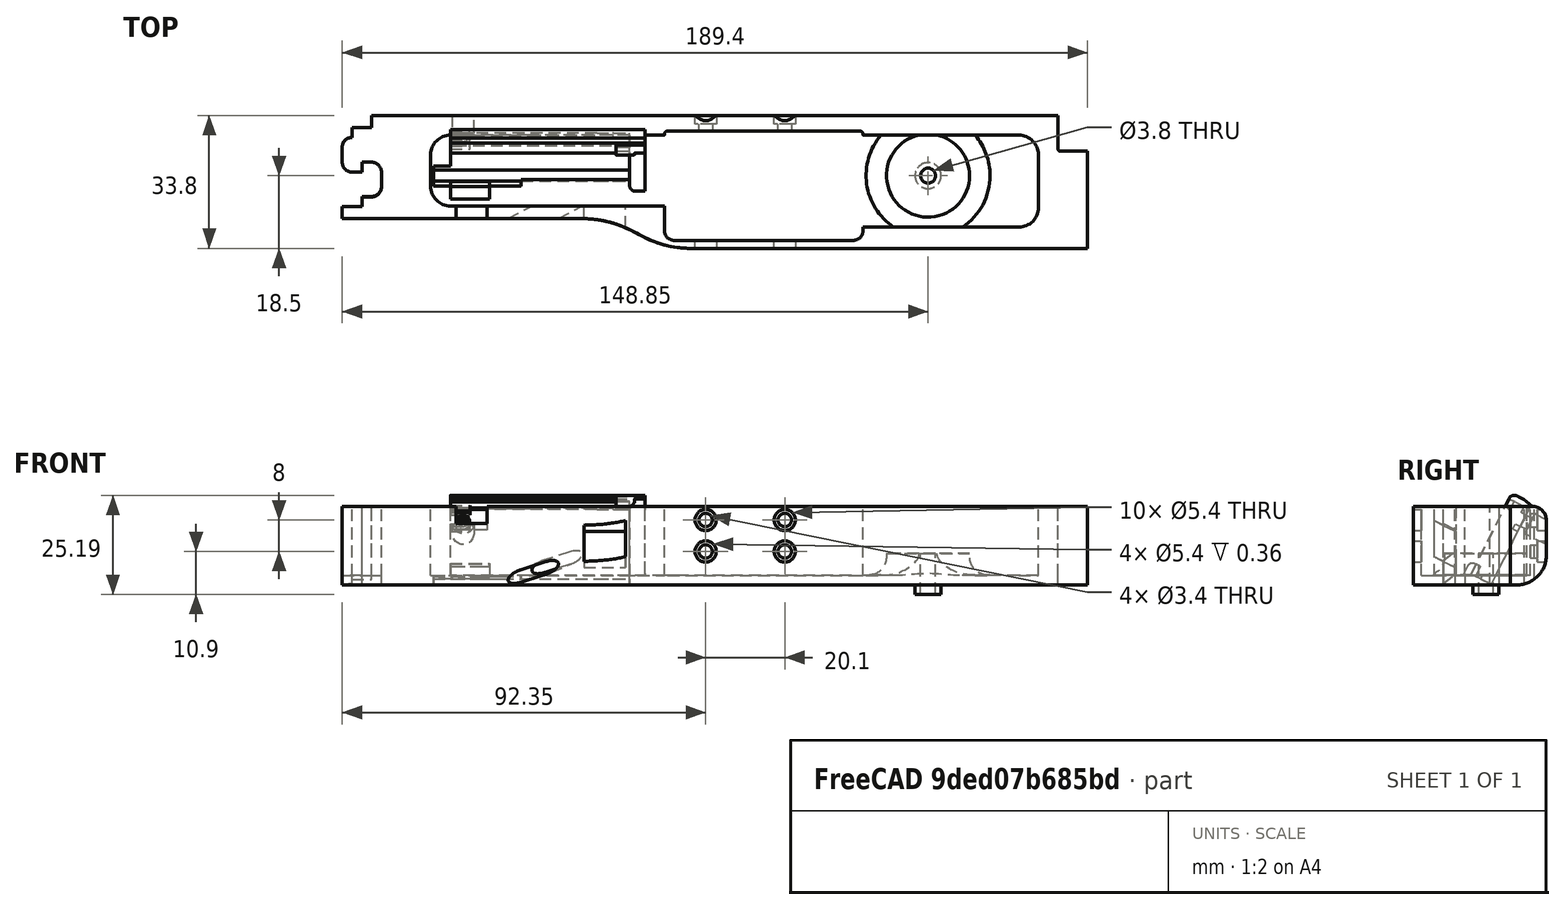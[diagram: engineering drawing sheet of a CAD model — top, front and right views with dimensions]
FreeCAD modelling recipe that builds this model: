
FCSTD DOCUMENT  (FreeCAD 0.19R0.19.2)
Label: v0_997
License: All rights reserved
LicenseURL: http://en.wikipedia.org/wiki/All_rights_reserved
objects: Sketcher::SketchObject×37, Part::Extrusion×31, Part::MultiFuse×19, Part::Cut×15, Part::Box×14, Part::Fillet×11, App::MeasureDistance×4, Part::Cylinder×4, Part::Revolution×1, Mesh::Feature×1
note: 132 computed .brp shape members not serialized (recipe doc carries the construction recipe); baked Part::Feature solids carry a one-line shape summary decoded from their .brp

FEATURE [Sketcher::SketchObject] Sketch
  FullyConstrained = true
  sketch-geometry (36):
    g0: LineSegment StartX=0 StartY=0 StartZ=0 EndX=154.4 EndY=0 EndZ=0
    g1: LineSegment StartX=154.4 StartY=0 StartZ=0 EndX=154.4 EndY=-7.6 EndZ=0
    g2: LineSegment StartX=32.5209 StartY=-26.2 StartZ=0 EndX=-7.5 EndY=-26.2 EndZ=0
    g3-g7: Circle x5 (B-spline internal-alignment scaffolding for g8; pole/knot coordinates omitted)
    g8: BSplineCurve PolesCount=5 KnotsCount=3 Degree=3 IsPeriodic=0
    g9: GeomPoint X=61.85 Y=-33.8 Z=0
    g10: GeomPoint X=47.185 Y=-29.9 Z=0
    g11: GeomPoint X=32.5209 Y=-26.2 Z=0
    g12: Circle CenterX=121.35 CenterY=-14.3 CenterZ=0 NormalX=0 NormalY=0 NormalZ=1 AngleXU=0 Radius=3.25
    g13: LineSegment StartX=-7.5 StartY=-26.2 StartZ=0 EndX=-27.5 EndY=-26.2 EndZ=0
    g14: LineSegment StartX=-20 StartY=0 StartZ=0 EndX=0 EndY=0 EndZ=0
    g15: LineSegment StartX=-25 StartY=-3.1 StartZ=0 EndX=-20 EndY=-3.1 EndZ=0
    g16: LineSegment StartX=-25 StartY=-3.1 StartZ=0 EndX=-25 EndY=-5.6 EndZ=0
    g17: LineSegment StartX=-27.5 StartY=-8.1 StartZ=0 EndX=-27.5 EndY=-11.85 EndZ=0
    g18: ArcOfCircle CenterX=-25 CenterY=-8.1 CenterZ=0 NormalX=0 NormalY=0 NormalZ=1 AngleXU=0 Radius=2.5 StartAngle=1.5708 EndAngle=3.14159
    g19: LineSegment StartX=-25 StartY=-14.35 StartZ=0 EndX=-22.5 EndY=-14.35 EndZ=0
    g20: ArcOfCircle CenterX=-25 CenterY=-11.85 CenterZ=0 NormalX=0 NormalY=0 NormalZ=1 AngleXU=0 Radius=2.5 StartAngle=3.14159 EndAngle=4.71239
    g21: LineSegment StartX=-22.5 StartY=-14.35 StartZ=0 EndX=-22.5 EndY=-11.85 EndZ=0
    g22: LineSegment StartX=-22.5 StartY=-11.85 StartZ=0 EndX=-20 EndY=-11.85 EndZ=0
    g23: ArcOfCircle CenterX=-20 CenterY=-14.35 CenterZ=0 NormalX=0 NormalY=0 NormalZ=1 AngleXU=0 Radius=2.5 StartAngle=8e-16 EndAngle=1.5708
    g24: LineSegment StartX=-17.5 StartY=-14.35 StartZ=0 EndX=-17.5 EndY=-18.1 EndZ=0
    g25: ArcOfCircle CenterX=-20 CenterY=-18.1 CenterZ=0 NormalX=0 NormalY=0 NormalZ=1 AngleXU=0 Radius=2.5 StartAngle=4.71239 EndAngle=6.28319
    g26: LineSegment StartX=-22.5 StartY=-20.6 StartZ=0 EndX=-20 EndY=-20.6 EndZ=0
    g27: LineSegment StartX=-22.5 StartY=-20.6 StartZ=0 EndX=-22.5 EndY=-23.1 EndZ=0
    g28: LineSegment StartX=-27.5 StartY=-23.1 StartZ=0 EndX=-22.5 EndY=-23.1 EndZ=0
    g29: LineSegment StartX=-20 StartY=-3.1 StartZ=0 EndX=-20 EndY=0 EndZ=0
    g30: LineSegment StartX=-27.5 StartY=-23.1 StartZ=0 EndX=-27.5 EndY=-26.2 EndZ=0
    g31: LineSegment StartX=154.4 StartY=-7.6 StartZ=0 EndX=154.4 EndY=-8.6 EndZ=0
    g32: ArcOfCircle CenterX=154.9 CenterY=-8.6 CenterZ=0 NormalX=0 NormalY=0 NormalZ=1 AngleXU=0 Radius=0.5 StartAngle=3.14159 EndAngle=4.71239
    g33: LineSegment StartX=154.9 StartY=-9.1 StartZ=0 EndX=161.9 EndY=-9.1 EndZ=0
    g34: LineSegment StartX=161.9 StartY=-9.1 StartZ=0 EndX=161.9 EndY=-33.8 EndZ=0
    g35: LineSegment StartX=161.9 StartY=-33.8 StartZ=0 EndX=61.85 EndY=-33.8 EndZ=0
  constraints (72):
    c: PointOnObject(g0,g-2)
    c: Horizontal(g0)
    c: Distance(g0) = 154.4
    c: DistanceY(g-1,g0) = 0
    c: Vertical(g1)
    c: Distance(g1) = 7.6
    c: Coincident(g1,g0)
    c: Horizontal(g2)
    c: Block(g2)
    c: Weight(g3) = 1
    c: Coincident(g8,g2)
    c: InternalAlignment(g3-g7 -> g8) x5
    c: InternalAlignment(g9,g8)
    c: InternalAlignment(g10,g8)
    c: InternalAlignment(g11,g8)
    c: Block(g12)
    c: Coincident(g13,g2)
    c: Horizontal(g13)
    c: Distance(g13) = 20
    c: Horizontal(g14)
    c: Distance(g14) = 20
    c: Coincident(g14,g0)
    c: Horizontal(g15)
    c: Vertical(g16)
    c: Coincident(g16,g15)
    c: Vertical(g17)
    c: Coincident(g18,g16)
    c: Block(g18)
    c: Coincident(g17,g18)
    c: Horizontal(g19)
    c: Coincident(g20,g17)
    c: Block(g20)
    c: Block(g19)
    c: Vertical(g21)
    c: Coincident(g21,g19)
    c: Horizontal(g22)
    c: Coincident(g22,g21)
    c: Coincident(g23,g22)
    c: Vertical(g24)
    c: Block(g23)
    c: Coincident(g24,g23)
    c: Coincident(g25,g24)
    c: Block(g25)
    c: Horizontal(g26)
    c: Coincident(g26,g25)
    c: Vertical(g27)
    c: Coincident(g27,g26)
    c: Horizontal(g28)
    c: Coincident(g28,g27)
    c: Block(g15)
    c: Block(g28)
    c: Coincident(g29,g15)
    c: Coincident(g29,g14)
    c: Vertical(g29)
    c: Coincident(g30,g28)
    c: Coincident(g30,g13)
    c: Vertical(g30)
    c: Vertical(g31)
    c: Distance(g31) = 1
    c: Coincident(g31,g1)
    c: Coincident(g32,g31)
    c: Block(g32)
    c: Coincident(g33,g32)
    c: Horizontal(g33)
    c: Coincident(g34,g33)
    c: Vertical(g34)
    c: Block(g34)
    c: Coincident(g35,g34)
    c: Horizontal(g35)
    c: Block(g35)
    c: Coincident(g8,g35)
    c: Block(g8)
FEATURE [Part::Extrusion] Extrude  label="mainBodyBaseExtrude"
  Base = -> Sketch
  Dir = (0,0,1)
  DirMode = 2
  FaceMakerClass = Part::FaceMakerBullseye
  LengthFwd = 2.4
  LengthRev = 0
  Solid = true
  Symmetric = false
FEATURE [Sketcher::SketchObject] Sketch001
  FullyConstrained = true
  sketch-geometry (75):
    g0: ArcOfCircle CenterX=144.4 CenterY=-10 CenterZ=0 NormalX=0 NormalY=0 NormalZ=1 AngleXU=0 Radius=5 StartAngle=4.345e-13 EndAngle=1.5708
    g1: LineSegment StartX=32.5209 StartY=-26.2 StartZ=0 EndX=-7.49911 EndY=-26.2 EndZ=0
    g2: LineSegment StartX=0 StartY=0 StartZ=0 EndX=154.4 EndY=0 EndZ=0
    g3-g7: Circle x5 (B-spline internal-alignment scaffolding for g8; pole/knot coordinates omitted)
    g8: BSplineCurve PolesCount=5 KnotsCount=3 Degree=3 IsPeriodic=0
    g9: GeomPoint X=61.85 Y=-33.8 Z=0
    g10: GeomPoint X=47.1857 Y=-29.9 Z=0
    g11: GeomPoint X=32.5209 Y=-26.2 Z=0
    g12: LineSegment StartX=154.4 StartY=0 StartZ=0 EndX=154.4 EndY=-7.6 EndZ=0
    g13: LineSegment StartX=20 StartY=-5 StartZ=0 EndX=54.35 EndY=-5 EndZ=0
    g14: LineSegment StartX=104.85 StartY=-5 StartZ=0 EndX=144.4 EndY=-5 EndZ=0
    g15: LineSegment StartX=54.35 StartY=-23 StartZ=0 EndX=20 EndY=-23 EndZ=0
    g16: LineSegment StartX=-27.4991 StartY=-26.2 StartZ=0 EndX=-7.49911 EndY=-26.2 EndZ=0
    g17: LineSegment StartX=-20 StartY=0 StartZ=0 EndX=0 EndY=0 EndZ=0
    g18: LineSegment StartX=-27.4991 StartY=-23.2 StartZ=0 EndX=-22.5 EndY=-23.2 EndZ=0
    g19: LineSegment StartX=-22.5 StartY=-20.7 StartZ=0 EndX=-22.5 EndY=-23.2 EndZ=0
    g20: LineSegment StartX=-22.5 StartY=-20.7 StartZ=0 EndX=-20 EndY=-20.7 EndZ=0
    g21: ArcOfCircle CenterX=-20 CenterY=-18.2 CenterZ=0 NormalX=0 NormalY=0 NormalZ=1 AngleXU=0 Radius=2.5 StartAngle=4.71239 EndAngle=6.28319
    g22: LineSegment StartX=-17.5 StartY=-14.4 StartZ=0 EndX=-17.5 EndY=-18.2 EndZ=0
    g23: ArcOfCircle CenterX=-20 CenterY=-14.4 CenterZ=0 NormalX=0 NormalY=0 NormalZ=1 AngleXU=0 Radius=2.5 StartAngle=9e-16 EndAngle=1.5708
    g24: LineSegment StartX=-22.5 StartY=-11.9 StartZ=0 EndX=-20 EndY=-11.9 EndZ=0
    g25: LineSegment StartX=-22.5 StartY=-14.4 StartZ=0 EndX=-22.5 EndY=-11.9 EndZ=0
    g26: LineSegment StartX=-25 StartY=-14.4 StartZ=0 EndX=-22.5 EndY=-14.4 EndZ=0
    g27: ArcOfCircle CenterX=-25 CenterY=-11.9 CenterZ=0 NormalX=0 NormalY=0 NormalZ=1 AngleXU=0 Radius=2.5 StartAngle=3.14159 EndAngle=4.71239
    g28: LineSegment StartX=-27.5 StartY=-8.1 StartZ=0 EndX=-27.5 EndY=-11.9 EndZ=0
    g29: ArcOfCircle CenterX=-25 CenterY=-8.1 CenterZ=0 NormalX=0 NormalY=0 NormalZ=1 AngleXU=0 Radius=2.5 StartAngle=1.5708 EndAngle=3.14159
    g30: LineSegment StartX=-25 StartY=-3.1 StartZ=0 EndX=-25 EndY=-5.6 EndZ=0
    g31: LineSegment StartX=-20 StartY=-3.1 StartZ=0 EndX=-25 EndY=-3.1 EndZ=0
    g32: LineSegment StartX=-20 StartY=0 StartZ=0 EndX=-20 EndY=-3.1 EndZ=0
    g33: LineSegment StartX=-27.4991 StartY=-26.2 StartZ=0 EndX=-27.4991 EndY=-23.2 EndZ=0
    g34: LineSegment StartX=4.09e-14 StartY=-5 StartZ=0 EndX=20 EndY=-5 EndZ=0
    g35: ArcOfCircle CenterX=7.1e-15 CenterY=-18 CenterZ=0 NormalX=0 NormalY=0 NormalZ=1 AngleXU=0 Radius=5 StartAngle=3.14159 EndAngle=4.71239
    g36: ArcOfCircle CenterX=4.26e-14 CenterY=-10 CenterZ=0 NormalX=0 NormalY=0 NormalZ=1 AngleXU=0 Radius=5 StartAngle=1.5708 EndAngle=3.14159
    g37: LineSegment StartX=-5 StartY=-18 StartZ=0 EndX=-5 EndY=-10 EndZ=0
    g38: LineSegment StartX=6.2e-15 StartY=-23 StartZ=0 EndX=20 EndY=-23 EndZ=0
    g39: LineSegment StartX=154.4 StartY=-7.6 StartZ=0 EndX=154.4 EndY=-8.6 EndZ=0
    g40: LineSegment StartX=154.9 StartY=-9.1 StartZ=0 EndX=161.9 EndY=-9.1 EndZ=0
    g41: ArcOfCircle CenterX=154.9 CenterY=-8.6 CenterZ=0 NormalX=0 NormalY=0 NormalZ=1 AngleXU=0 Radius=0.5 StartAngle=3.14159 EndAngle=4.71299
    g42: LineSegment StartX=104.85 StartY=-28.3916 StartZ=0 EndX=144.408 EndY=-28.3916 EndZ=0
    g43: LineSegment StartX=149.4 StartY=-10 StartZ=0 EndX=149.4 EndY=-23.4 EndZ=0
    g44: ArcOfCircle CenterX=144.408 CenterY=-23.4 CenterZ=0 NormalX=0 NormalY=0 NormalZ=1 AngleXU=0 Radius=4.99164 StartAngle=4.71239 EndAngle=6.28319
    g45: LineSegment StartX=104.85 StartY=-28.3916 StartZ=0 EndX=104.85 EndY=-28.7833 EndZ=0
    g46: LineSegment StartX=54.35 StartY=-28.7916 StartZ=0 EndX=54.35 EndY=-23 EndZ=0
    g47: LineSegment StartX=161.9 StartY=-33.8 StartZ=0 EndX=161.9 EndY=-9.1 EndZ=0
    g48: LineSegment StartX=61.85 StartY=-33.8 StartZ=0 EndX=161.9 EndY=-33.8 EndZ=0
    g49: Circle CenterX=54.35 CenterY=-28.7916 CenterZ=0 NormalX=0 NormalY=0 NormalZ=1 AngleXU=0 Radius=1
    g50: Circle CenterX=54.35 CenterY=-31.7916 CenterZ=0 NormalX=0 NormalY=0 NormalZ=1 AngleXU=0 Radius=1
    g51: Circle CenterX=57.35 CenterY=-31.7916 CenterZ=0 NormalX=0 NormalY=0 NormalZ=1 AngleXU=0 Radius=1
    g52: BSplineCurve PolesCount=3 KnotsCount=2 Degree=2 IsPeriodic=0
    g53: GeomPoint X=54.35 Y=-28.7916 Z=0
    g54: GeomPoint X=57.35 Y=-31.7916 Z=0
    g55: Circle CenterX=104.85 CenterY=-28.7833 CenterZ=0 NormalX=0 NormalY=0 NormalZ=1 AngleXU=0 Radius=1
    g56: Circle CenterX=104.85 CenterY=-31.7916 CenterZ=0 NormalX=0 NormalY=0 NormalZ=1 AngleXU=0 Radius=1
    g57: Circle CenterX=101.85 CenterY=-31.7916 CenterZ=0 NormalX=0 NormalY=0 NormalZ=1 AngleXU=0 Radius=1
    g58: BSplineCurve PolesCount=3 KnotsCount=2 Degree=2 IsPeriodic=0
    g59: GeomPoint X=104.85 Y=-28.7833 Z=0
    g60: GeomPoint X=101.85 Y=-31.7916 Z=0
    g61: LineSegment StartX=57.35 StartY=-31.7916 StartZ=0 EndX=101.85 EndY=-31.7916 EndZ=0
    g62: Circle CenterX=54.35 CenterY=-5 CenterZ=0 NormalX=0 NormalY=0 NormalZ=1 AngleXU=0 Radius=1
    g63: Circle CenterX=54.35 CenterY=-4 CenterZ=0 NormalX=0 NormalY=0 NormalZ=1 AngleXU=0 Radius=1
    g64: Circle CenterX=55.15 CenterY=-4 CenterZ=0 NormalX=0 NormalY=0 NormalZ=1 AngleXU=0 Radius=1
    g65: BSplineCurve PolesCount=3 KnotsCount=2 Degree=2 IsPeriodic=0
    g66: GeomPoint X=54.35 Y=-5 Z=0
    g67: GeomPoint X=55.15 Y=-4 Z=0
    g68: Circle CenterX=104.85 CenterY=-5 CenterZ=0 NormalX=0 NormalY=0 NormalZ=1 AngleXU=0 Radius=1
    g69: Circle CenterX=104.85 CenterY=-4 CenterZ=0 NormalX=0 NormalY=0 NormalZ=1 AngleXU=0 Radius=1
    g70: Circle CenterX=104.05 CenterY=-4 CenterZ=0 NormalX=0 NormalY=0 NormalZ=1 AngleXU=0 Radius=1
    g71: BSplineCurve PolesCount=3 KnotsCount=2 Degree=2 IsPeriodic=0
    g72: GeomPoint X=104.85 Y=-5 Z=0
    g73: GeomPoint X=104.05 Y=-4 Z=0
    g74: LineSegment StartX=104.05 StartY=-4 StartZ=0 EndX=55.15 EndY=-4 EndZ=0
  constraints (156):
    c: PointOnObject(g2,g-2)
    c: DistanceY(g-1,g2) = 0
    c: Block(g0)
    c: Horizontal(g1)
    c: Distance(g1) = 40.02
    c: Horizontal(g2)
    c: Block(g2)
    c: Weight(g3) = 1
    c: Equal(g3, g4-g7) x4
    c: Coincident(g8,g1)
    c: InternalAlignment(g3-g7 -> g8) x5
    c: InternalAlignment(g9,g8)
    c: InternalAlignment(g10,g8)
    c: InternalAlignment(g11,g8)
    c: Vertical(g12)
    c: Coincident(g12,g2)
    c: Distance(g12) = 7.6
    c: Block(g12)
    c: Horizontal(g13)
    c: Coincident(g14,g0)
    c: Horizontal(g14)
    c: Horizontal(g15)
    c: Horizontal(g16)
    c: Distance(g16) = 20
    c: Coincident(g1,g16)
    c: Horizontal(g17)
    c: Distance(g17) = 20
    c: Coincident(g17,g2)
    c: Horizontal(g31)
    c: Vertical(g30)
    c: Coincident(g29,g30)
    c: Vertical(g28)
    c: Block(g29)
    c: Coincident(g27,g28)
    c: Block(g27)
    c: Horizontal(g26)
    c: Coincident(g26,g27)
    c: Vertical(g25)
    c: Coincident(g25,g26)
    c: Horizontal(g24)
    c: Coincident(g23,g24)
    c: Block(g23)
    c: Vertical(g22)
    c: Coincident(g21,g22)
    c: Block(g21)
    c: Horizontal(g20)
    c: Coincident(g20,g21)
    c: Vertical(g19)
    c: Coincident(g19,g20)
    c: Horizontal(g18)
    c: Coincident(g18,g19)
    c: Coincident(g32,g17)
    c: Coincident(g32,g31)
    c: Vertical(g32)
    c: Coincident(g33,g16)
    c: Coincident(g33,g18)
    c: Vertical(g33)
    c: Block(g33)
    c: Block(g18)
    c: Block(g22)
    c: Block(g26)
    c: Block(g25)
    c: Block(g24)
    c: Block(g28)
    c: Block(g31)
    c: Block(g30)
    c: Horizontal(g34)
    c: Distance(g34) = 20
    c: Block(g35)
    c: Block(g36)
    c: Coincident(g37,g35)
    c: Coincident(g37,g36)
    c: Vertical(g37)
    c: Coincident(g38,g35)
    c: Coincident(g38,g15)
    c: Horizontal(g38)
    c: Block(g38)
    c: Block(g34)
    c: Block(g13)
    c: Vertical(g39)
    c: Distance(g39) = 1
    c: Coincident(g39,g12)
    c: Horizontal(g40)
    c: Coincident(g41,g39)
    c: Coincident(g41,g40)
    c: Block(g39)
    c: Block(g41)
    c: Horizontal(g42)
    c: Vertical(g43)
    c: Distance(g43) = 13.4
    c: Coincident(g43,g0)
    c: Block(g42)
    c: Block(g43)
    c: Coincident(g44,g43)
    c: Coincident(g44,g42)
    c: Block(g44)
    c: Distance(g15) = 34.35
    c: Coincident(g45,g42)
    c: Vertical(g45)
    c: Coincident(g46,g15)
    c: Vertical(g46)
    c: Coincident(g47,g40)
    c: Vertical(g47)
    c: Block(g47)
    c: Coincident(g48,g47)
    c: Horizontal(g48)
    c: Block(g48)
    c: Coincident(g8,g48)
    c: Block(g8)
    c: Coincident(g52,g46)
    c: Weight(g49) = 1
    c: Equal(g49,g50)
    c: Equal(g49,g51)
    c: InternalAlignment(g49,g52)
    c: InternalAlignment(g50,g52)
    c: InternalAlignment(g51,g52)
    c: InternalAlignment(g53,g52)
    c: InternalAlignment(g54,g52)
    c: Coincident(g58,g45)
    c: Weight(g55) = 1
    c: Equal(g55,g56)
    c: Equal(g55,g57)
    c: InternalAlignment(g55,g58)
    c: InternalAlignment(g56,g58)
    c: InternalAlignment(g57,g58)
    c: InternalAlignment(g59,g58)
    c: InternalAlignment(g60,g58)
    c: Block(g58)
    c: Block(g52)
    c: Coincident(g61,g52)
    c: Coincident(g61,g58)
    c: Horizontal(g61)
    c: Block(g14)
    c: Coincident(g65,g13)
    c: Weight(g62) = 1
    c: Equal(g62,g63)
    c: Equal(g62,g64)
    c: InternalAlignment(g62,g65)
    c: InternalAlignment(g63,g65)
    c: InternalAlignment(g64,g65)
    c: InternalAlignment(g66,g65)
    c: InternalAlignment(g67,g65)
    c: Block(g65)
    c: Coincident(g71,g14)
    c: Weight(g68) = 1
    c: Equal(g68,g69)
    c: Equal(g68,g70)
    c: InternalAlignment(g68,g71)
    c: InternalAlignment(g69,g71)
    c: InternalAlignment(g70,g71)
    c: InternalAlignment(g72,g71)
    c: InternalAlignment(g73,g71)
    c: Block(g71)
    c: Coincident(g74,g71)
    c: Coincident(g74,g65)
    c: Horizontal(g74)
FEATURE [Sketcher::SketchObject] Sketch005
  FullyConstrained = true
  Placement = pos=(0,0,0) rot=(1,0,0;1.5708rad)
  sketch-geometry (4):
    g0: Circle CenterX=84.95 CenterY=16.5 CenterZ=0 NormalX=0 NormalY=0 NormalZ=1 AngleXU=0 Radius=1.7
    g1: Circle CenterX=84.95 CenterY=8.5 CenterZ=0 NormalX=0 NormalY=0 NormalZ=1 AngleXU=0 Radius=1.7
    g2: Circle CenterX=64.85 CenterY=8.5 CenterZ=0 NormalX=0 NormalY=0 NormalZ=1 AngleXU=0 Radius=1.7
    g3: Circle CenterX=64.85 CenterY=16.5 CenterZ=0 NormalX=0 NormalY=0 NormalZ=1 AngleXU=0 Radius=1.7
  constraints (4):
    c: Block(g0)
    c: Block(g1)
    c: Block(g2)
    c: Block(g3)
FEATURE [Part::Extrusion] Extrude004  label="removeFromMainBodyToCreateScrewHolesForSolenoidExtrude004"
  Base = -> Sketch005
  Dir = (0,-1,1.1e-15)
  DirMode = 2
  FaceMakerClass = Part::FaceMakerBullseye
  LengthFwd = 10
  LengthRev = 0
  Solid = true
  Symmetric = false
FEATURE [Sketcher::SketchObject] Sketch004
  FullyConstrained = true
  Placement = pos=(0,0,0) rot=(1,0,0;1.5708rad)
  sketch-geometry (12):
    g0: LineSegment StartX=15.75 StartY=2.5 StartZ=0 EndX=15.75 EndY=0 EndZ=0
    g1: Circle CenterX=15.75 CenterY=2.5 CenterZ=0 NormalX=0 NormalY=0 NormalZ=1 AngleXU=0 Radius=1
    g2: Circle CenterX=10.55 CenterY=2.5 CenterZ=0 NormalX=0 NormalY=0 NormalZ=1 AngleXU=0 Radius=1
    g3: Circle CenterX=10.55 CenterY=8 CenterZ=0 NormalX=0 NormalY=0 NormalZ=1 AngleXU=0 Radius=1
    g4: BSplineCurve PolesCount=3 KnotsCount=2 Degree=2 IsPeriodic=0
    g5: GeomPoint X=15.75 Y=2.5 Z=0
    g6: GeomPoint X=10.55 Y=8 Z=0
    g7: LineSegment StartX=1.9 StartY=8 StartZ=0 EndX=10.55 EndY=8 EndZ=0
    g8: LineSegment StartX=1.9 StartY=-2.4 StartZ=0 EndX=1.9 EndY=8 EndZ=0
    g9: LineSegment StartX=3.30092 StartY=-2.4 StartZ=0 EndX=3.30092 EndY=0 EndZ=0
    g10: LineSegment StartX=15.75 StartY=0 StartZ=0 EndX=3.30092 EndY=0 EndZ=0
    g11: LineSegment StartX=3.30092 StartY=-2.4 StartZ=0 EndX=1.9 EndY=-2.4 EndZ=0
  constraints (26):
    c: Vertical(g0)
    c: Distance(g0) = 2.5
    c: Coincident(g4,g0)
    c: Weight(g1) = 1
    c: Equal(g1,g2)
    c: Equal(g1,g3)
    c: InternalAlignment(g1,g4)
    c: InternalAlignment(g2,g4)
    c: InternalAlignment(g3,g4)
    c: InternalAlignment(g5,g4)
    c: InternalAlignment(g6,g4)
    c: Block(g4)
    c: Coincident(g7,g4)
    c: Horizontal(g7)
    c: Vertical(g8)
    c: Coincident(g8,g7)
    c: Block(g8)
    c: Vertical(g9)
    c: Coincident(g10,g0)
    c: PointOnObject(g10,g-1)
    c: Horizontal(g10)
    c: Coincident(g10,g9)
    c: Block(g9)
    c: Coincident(g11,g9)
    c: Coincident(g11,g8)
    c: Horizontal(g11)
FEATURE [Sketcher::SketchObject] Sketch007
  FullyConstrained = true
  Placement = pos=(0,-14.3,2.37) rot=(-1,0,0;2.03453rad)
  sketch-geometry (6):
    g0: LineSegment StartX=0 StartY=0 StartZ=0 EndX=45.5 EndY=0 EndZ=0
    g1: LineSegment StartX=0 StartY=0 StartZ=0 EndX=0 EndY=-21.2 EndZ=0
    g2: LineSegment StartX=45.5 StartY=0 StartZ=0 EndX=49.5 EndY=0 EndZ=0
    g3: LineSegment StartX=49.5 StartY=0 StartZ=0 EndX=49.5 EndY=-21.2 EndZ=0
    g4: LineSegment StartX=49.5 StartY=-21.2 StartZ=0 EndX=0 EndY=-21.2 EndZ=0
    g5: Circle CenterX=3.25 CenterY=-18.05 CenterZ=0 NormalX=0 NormalY=0 NormalZ=1 AngleXU=0 Radius=1.6
  constraints (15):
    c: Coincident(g0,g-1)
    c: Horizontal(g0)
    c: Distance(g0) = 45.5
    c: Coincident(g1,g0)
    c: Vertical(g1)
    c: Horizontal(g2)
    c: Distance(g2) = 4
    c: Coincident(g2,g0)
    c: Coincident(g3,g2)
    c: Vertical(g3)
    c: Block(g3)
    c: Coincident(g4,g3)
    c: Horizontal(g4)
    c: Coincident(g4,g1)
    c: Block(g5)
FEATURE [Part::Extrusion] Extrude005  label="solenoidDriverHolderExtrude005"
  Base = -> Sketch007
  Dir = (0,0.894389,-0.447291)
  DirMode = 2
  FaceMakerClass = Part::FaceMakerBullseye
  LengthFwd = 10
  LengthRev = 0
  Placement = pos=(0,0,-2) rot=(0,0,1;0rad)
  Solid = true
  Symmetric = false
FEATURE [Sketcher::SketchObject] Sketch008
  FullyConstrained = false
  Placement = pos=(0,-4.3,-2.6) rot=(-1,0,0;2.03453rad)
  sketch-geometry (1):
    g0: Circle CenterX=42.25 CenterY=-3.15 CenterZ=0 NormalX=0 NormalY=0 NormalZ=1 AngleXU=0 Radius=4.5
FEATURE [Sketcher::SketchObject] Sketch009
  FullyConstrained = true
  Placement = pos=(0,-4.3,-2.6) rot=(-1,0,0;2.03453rad)
  sketch-geometry (1):
    g0: Circle CenterX=3.25 CenterY=-18.0217 CenterZ=0 NormalX=0 NormalY=0 NormalZ=1 AngleXU=0 Radius=2.8
  constraints (1):
    c: Block(g0)
FEATURE [Sketcher::SketchObject] Sketch010
  FullyConstrained = true
  Placement = pos=(0,-14.3,2.37) rot=(-1,0,0;2.03453rad)
  sketch-geometry (1):
    g0: Circle CenterX=3.25 CenterY=-18.05 CenterZ=0 NormalX=0 NormalY=0 NormalZ=1 AngleXU=0 Radius=1.6
  constraints (1):
    c: Block(g0)
FEATURE [Part::Extrusion] Extrude008  label="removeFromScrewHole3"
  Base = -> Sketch010
  Dir = (0,0.894389,-0.447291)
  DirMode = 2
  FaceMakerClass = Part::FaceMakerBullseye
  LengthFwd = -25
  LengthRev = 0
  Placement = pos=(0,4,-4) rot=(0,0,1;0rad)
  Solid = true
  Symmetric = false
FEATURE [Sketcher::SketchObject] Sketch011
  FullyConstrained = true
  Placement = pos=(0,-14.3,2.37) rot=(-1,0,0;2.03453rad)
  sketch-geometry (4):
    g0: LineSegment StartX=49.5 StartY=-21.2 StartZ=0 EndX=49.5 EndY=-22.8 EndZ=0
    g1: LineSegment StartX=49.5 StartY=-22.8 StartZ=0 EndX=0.002238 EndY=-22.8 EndZ=0
    g2: LineSegment StartX=0.002238 StartY=-21.2 StartZ=0 EndX=0.002238 EndY=-22.8 EndZ=0
    g3: LineSegment StartX=49.5 StartY=-21.2 StartZ=0 EndX=0.002238 EndY=-21.2 EndZ=0
  constraints (10):
    c: Vertical(g0)
    c: Distance(g0) = 1.6
    c: Coincident(g1,g0)
    c: Horizontal(g1)
    c: Vertical(g2)
    c: Coincident(g2,g1)
    c: Coincident(g3,g0)
    c: Coincident(g3,g2)
    c: Horizontal(g3)
    c: Block(g3)
FEATURE [Part::Extrusion] Extrude009  label="solenoidDriverTopLipFront"
  Base = -> Sketch011
  Dir = (0,0.894389,-0.447291)
  DirMode = 2
  FaceMakerClass = Part::FaceMakerBullseye
  LengthFwd = -2
  LengthRev = 0
  Placement = pos=(0,-2.9,-0.35) rot=(0,0,1;0rad)
  Solid = true
  Symmetric = false
FEATURE [Sketcher::SketchObject] Sketch012
  FullyConstrained = true
  Placement = pos=(0,-14.3,2.37) rot=(-1,0,0;2.03453rad)
  sketch-geometry (4):
    g0: LineSegment StartX=49.5 StartY=-21.2 StartZ=0 EndX=49.5 EndY=-22.8 EndZ=0
    g1: LineSegment StartX=49.5 StartY=-22.8 StartZ=0 EndX=0.002238 EndY=-22.8 EndZ=0
    g2: LineSegment StartX=0.002238 StartY=-21.2 StartZ=0 EndX=0.002238 EndY=-22.8 EndZ=0
    g3: LineSegment StartX=49.5 StartY=-21.2 StartZ=0 EndX=0.002238 EndY=-21.2 EndZ=0
  constraints (10):
    c: Vertical(g0)
    c: Distance(g0) = 1.6
    c: Coincident(g1,g0)
    c: Horizontal(g1)
    c: Vertical(g2)
    c: Coincident(g2,g1)
    c: Coincident(g3,g0)
    c: Coincident(g3,g2)
    c: Horizontal(g3)
    c: Block(g3)
FEATURE [Part::Extrusion] Extrude010  label="solenoidDriverTopLipLowerExtrude010"
  Base = -> Sketch012
  Dir = (0,0.894389,-0.447291)
  DirMode = 2
  FaceMakerClass = Part::FaceMakerBullseye
  LengthFwd = 5.05
  LengthRev = 0
  Solid = true
  Symmetric = false
FEATURE [Sketcher::SketchObject] Sketch015
  FullyConstrained = true
  Placement = pos=(0,-14.3,2.37) rot=(-1,0,0;2.03453rad)
  sketch-geometry (4):
    g0: LineSegment StartX=0 StartY=1.5 StartZ=0 EndX=0 EndY=0 EndZ=0
    g1: LineSegment StartX=0 StartY=1.5 StartZ=0 EndX=5 EndY=1.5 EndZ=0
    g2: LineSegment StartX=5 StartY=1.5 StartZ=0 EndX=5 EndY=0 EndZ=0
    g3: LineSegment StartX=0 StartY=0 StartZ=0 EndX=5 EndY=0 EndZ=0
  constraints (13):
    c: Vertical(g0)
    c: Distance(g0) = 1.5
    c: Horizontal(g1)
    c: Distance(g1) = 5
    c: Coincident(g1,g0)
    c: Vertical(g2)
    c: Distance(g2) = 1.5
    c: Coincident(g2,g1)
    c: Block(g1)
    c: Block(g2)
    c: Block(g0)
    c: Coincident(g3,g0)
    c: Coincident(g3,g2)
FEATURE [Part::Extrusion] Extrude013  label="solenoidDriverBottomLipTopExtrude012"
  Base = -> Sketch015
  Dir = (0,0.894389,-0.447291)
  DirMode = 2
  FaceMakerClass = Part::FaceMakerBullseye
  LengthFwd = -6.5
  LengthRev = 0
  Placement = pos=(0,-14.15,19.65) rot=(1,0,0;1.5708rad)
  Solid = true
  Symmetric = false
FEATURE [Sketcher::SketchObject] Sketch016
  FullyConstrained = true
  Placement = pos=(0,0,0) rot=(1,0,0;1.5708rad)
  sketch-geometry (4):
    g0: Circle CenterX=84.15 CenterY=16.5 CenterZ=0 NormalX=0 NormalY=0 NormalZ=1 AngleXU=0 Radius=2.7
    g1: Circle CenterX=64.05 CenterY=16.5 CenterZ=0 NormalX=0 NormalY=0 NormalZ=1 AngleXU=0 Radius=2.7
    g2: Circle CenterX=64.05 CenterY=8.5 CenterZ=0 NormalX=0 NormalY=0 NormalZ=1 AngleXU=0 Radius=2.7
    g3: Circle CenterX=84.15 CenterY=8.5 CenterZ=0 NormalX=0 NormalY=0 NormalZ=1 AngleXU=0 Radius=2.7
  constraints (4):
    c: Block(g0)
    c: Block(g1)
    c: Block(g3)
    c: Block(g2)
FEATURE [Part::Extrusion] Extrude014  label="removeFromMainBodyToCreateScrewHoleCounterSinks"
  Base = -> Sketch016
  Dir = (0,-1,1.1e-15)
  DirMode = 2
  FaceMakerClass = Part::FaceMakerBullseye
  LengthFwd = 1.9
  LengthRev = 0
  Placement = pos=(0.8,-0.36,0) rot=(0,0,1;0rad)
  Solid = true
  Symmetric = false
FEATURE [Part::Extrusion] Extrude015  label="removeFromScrewHole2Extrude007"
  Base = -> Sketch009
  Dir = (0,0.894389,-0.447291)
  DirMode = 2
  FaceMakerClass = Part::FaceMakerBullseye
  LengthFwd = 10
  LengthRev = 0
  Placement = pos=(0,-8,2) rot=(0,0,1;0rad)
  Solid = true
  Symmetric = false
FEATURE [Sketcher::SketchObject] Sketch017
  FullyConstrained = true
  Placement = pos=(0,-14.3,2.37) rot=(-1,0,0;2.03453rad)
  sketch-geometry (4):
    g0: LineSegment StartX=0 StartY=1.5 StartZ=0 EndX=0 EndY=0 EndZ=0
    g1: LineSegment StartX=0 StartY=1.5 StartZ=0 EndX=5 EndY=1.5 EndZ=0
    g2: LineSegment StartX=5 StartY=1.5 StartZ=0 EndX=5 EndY=0 EndZ=0
    g3: LineSegment StartX=0 StartY=0 StartZ=0 EndX=5 EndY=0 EndZ=0
  constraints (13):
    c: Vertical(g0)
    c: Distance(g0) = 1.5
    c: Horizontal(g1)
    c: Distance(g1) = 5
    c: Coincident(g1,g0)
    c: Vertical(g2)
    c: Distance(g2) = 1.5
    c: Coincident(g2,g1)
    c: Block(g1)
    c: Block(g2)
    c: Block(g0)
    c: Coincident(g3,g0)
    c: Coincident(g3,g2)
FEATURE [Part::Extrusion] Extrude016  label="solenoidDriverBottomLipTopExtrude013"
  Base = -> Sketch017
  Dir = (0,0.894389,-0.447291)
  DirMode = 2
  FaceMakerClass = Part::FaceMakerBullseye
  LengthFwd = -6.5
  LengthRev = 0
  Placement = pos=(0,-15.45,20.3) rot=(1,0,0;1.5708rad)
  Solid = true
  Symmetric = false
FEATURE [Part::Fillet] Fillet005  label="solenoidDriverBottomLipTopFillet005"
  Base = -> Extrude016
  Edges = 1 edges r=1.4: [Edge6]
FEATURE [Sketcher::SketchObject] Sketch018
  FullyConstrained = true
  Placement = pos=(38.5,-14.3,2.37) rot=(-1,0,0;2.03453rad)
  sketch-geometry (4):
    g0: LineSegment StartX=11 StartY=0 StartZ=0 EndX=11 EndY=1.5 EndZ=0
    g1: LineSegment StartX=11 StartY=0 StartZ=0 EndX=3.6 EndY=0 EndZ=0
    g2: LineSegment StartX=3.6 StartY=0 StartZ=0 EndX=3.6 EndY=1.5 EndZ=0
    g3: LineSegment StartX=11 StartY=1.5 StartZ=0 EndX=3.6 EndY=1.5 EndZ=0
  constraints (12):
    c: PointOnObject(g0,g-1)
    c: Vertical(g0)
    c: Distance(g0) = 1.5
    c: Horizontal(g1)
    c: Distance(g1) = 7.4
    c: Coincident(g1,g0)
    c: Block(g0)
    c: Coincident(g2,g1)
    c: Vertical(g2)
    c: Coincident(g3,g0)
    c: Horizontal(g3)
    c: Coincident(g2,g3)
FEATURE [Part::Extrusion] Extrude017
  Base = -> Sketch018
  Dir = (0,0.894389,-0.447291)
  DirMode = 2
  FaceMakerClass = Part::FaceMakerBullseye
  LengthFwd = 4
  LengthRev = 0
  Placement = pos=(0,-8.212,34.025) rot=(1,0,0;1.5708rad)
  Solid = true
  Symmetric = false
FEATURE [Sketcher::SketchObject] Sketch019
  FullyConstrained = true
  Placement = pos=(0,0,0) rot=(1,0,0;1.5708rad)
  sketch-geometry (4):
    g0: Circle CenterX=84.95 CenterY=8.5 CenterZ=0 NormalX=0 NormalY=0 NormalZ=1 AngleXU=0 Radius=2.7
    g1: Circle CenterX=64.85 CenterY=8.5 CenterZ=0 NormalX=0 NormalY=0 NormalZ=1 AngleXU=0 Radius=2.7
    g2: Circle CenterX=64.85 CenterY=16.5 CenterZ=0 NormalX=0 NormalY=0 NormalZ=1 AngleXU=0 Radius=2.7
    g3: Circle CenterX=84.95 CenterY=16.5 CenterZ=0 NormalX=0 NormalY=0 NormalZ=1 AngleXU=0 Radius=2.7
  constraints (4):
    c: Block(g3)
    c: Block(g2)
    c: Block(g0)
    c: Block(g1)
FEATURE [Part::Extrusion] Extrude019  label="removeSolenoidAdjusterHoles"
  Base = -> Sketch019
  Dir = (0,-1,1.1e-15)
  DirMode = 2
  FaceMakerClass = Part::FaceMakerBullseye
  LengthFwd = 6
  LengthRev = 0
  Placement = pos=(0,-30,0) rot=(0,0,1;0rad)
  Solid = true
  Symmetric = false
FEATURE [Sketcher::SketchObject] Sketch020
  FullyConstrained = true
  Placement = pos=(0,-14.3,2.37) rot=(-1,0,0;2.03453rad)
  sketch-geometry (6):
    g0: LineSegment StartX=45.5 StartY=-21.2 StartZ=0 EndX=49.5 EndY=-21.2 EndZ=0
    g1: LineSegment StartX=45.5 StartY=0 StartZ=0 EndX=49.5 EndY=0 EndZ=0
    g2: LineSegment StartX=49.5 StartY=0 StartZ=0 EndX=49.5 EndY=-21.2 EndZ=0
    g3: LineSegment StartX=4 StartY=0 StartZ=0 EndX=4 EndY=-21.2 EndZ=0
    g4: LineSegment StartX=45.5 StartY=-21.2 StartZ=0 EndX=4 EndY=-21.2 EndZ=0
    g5: LineSegment StartX=4 StartY=0 StartZ=0 EndX=45.5 EndY=0 EndZ=0
  constraints (16):
    c: Horizontal(g0)
    c: Distance(g0) = 4
    c: Horizontal(g1)
    c: Distance(g1) = 4
    c: Coincident(g2,g1)
    c: Coincident(g2,g0)
    c: Vertical(g2)
    c: Block(g2)
    c: Vertical(g3)
    c: Coincident(g4,g0)
    c: Horizontal(g4)
    c: Coincident(g4,g3)
    c: Coincident(g5,g1)
    c: Horizontal(g5)
    c: Block(g3)
    c: Block(g5)
FEATURE [Part::Box] Box  label="Cube"
  AttacherType = Attacher::AttachEngine3D
  Height = 10
  Length = 190
  Placement = pos=(-30,0,0) rot=(0,0,1;0rad)
  Width = 10
FEATURE [Part::Fillet] Fillet008
  Base = -> Box
  Edges = 1 edges r=7.5: [Edge11]
FEATURE [Part::Box] Box001  label="Cube001"
  AttacherType = Attacher::AttachEngine3D
  Height = 10
  Length = 190
  Placement = pos=(-35,0,0) rot=(0,0,1;0rad)
  Width = 10
FEATURE [Part::Cut] Cut  label="filletMain"
  Base = -> Box001
  Placement = pos=(0,-10,0) rot=(0,0,1;0rad)
  Tool = -> Fillet008
FEATURE [Part::Box] Box002  label="Cube002"
  AttacherType = Attacher::AttachEngine3D
  Height = 30
  Length = 190
  Placement = pos=(-20,0,0) rot=(0,0,1;0rad)
  Width = 10
FEATURE [Part::Box] Box003  label="Cube003"
  AttacherType = Attacher::AttachEngine3D
  Height = 10
  Length = 190
  Placement = pos=(-90,-50,-10) rot=(0,0,1;0rad)
  Width = 50
FEATURE [Sketcher::SketchObject] Sketch021
  FullyConstrained = true
  Placement = pos=(0,-14.3,2.37) rot=(-1,0,0;2.03453rad)
  sketch-geometry (6):
    g0: LineSegment StartX=41.65 StartY=-3.15 StartZ=0 EndX=38.95 EndY=-3.15 EndZ=0
    g1: LineSegment StartX=36.25 StartY=-3.15 StartZ=0 EndX=38.95 EndY=-3.15 EndZ=0
    g2: LineSegment StartX=41.65 StartY=-3.15 StartZ=0 EndX=41.65 EndY=-7.15 EndZ=0
    g3: LineSegment StartX=38.95 StartY=-7.15 StartZ=0 EndX=41.65 EndY=-7.15 EndZ=0
    g4: LineSegment StartX=38.95 StartY=-7.15 StartZ=0 EndX=36.25 EndY=-7.15 EndZ=0
    g5: LineSegment StartX=36.25 StartY=-3.15 StartZ=0 EndX=36.25 EndY=-7.15 EndZ=0
  constraints (16):
    c: Horizontal(g0)
    c: Distance(g0) = 2.7
    c: Horizontal(g1)
    c: Distance(g1) = 2.7
    c: Coincident(g1,g0)
    c: Block(g0)
    c: Coincident(g2,g0)
    c: Vertical(g2)
    c: Horizontal(g3)
    c: Coincident(g3,g2)
    c: Horizontal(g4)
    c: Coincident(g5,g1)
    c: Vertical(g5)
    c: Coincident(g5,g4)
    c: Block(g3)
    c: Block(g4)
FEATURE [Sketcher::SketchObject] Sketch022
  FullyConstrained = true
  Placement = pos=(0,-14.3,2.37) rot=(-1,0,0;2.03453rad)
  sketch-geometry (6):
    g0: LineSegment StartX=41.65 StartY=-3.15 StartZ=0 EndX=38.95 EndY=-3.15 EndZ=0
    g1: LineSegment StartX=36.25 StartY=-3.15 StartZ=0 EndX=38.95 EndY=-3.15 EndZ=0
    g2: LineSegment StartX=41.65 StartY=-3.15 StartZ=0 EndX=41.65 EndY=-7.15 EndZ=0
    g3: LineSegment StartX=38.95 StartY=-7.15 StartZ=0 EndX=41.65 EndY=-7.15 EndZ=0
    g4: LineSegment StartX=38.95 StartY=-7.15 StartZ=0 EndX=36.25 EndY=-7.15 EndZ=0
    g5: LineSegment StartX=36.25 StartY=-3.15 StartZ=0 EndX=36.25 EndY=-7.15 EndZ=0
  constraints (16):
    c: Horizontal(g0)
    c: Distance(g0) = 2.7
    c: Horizontal(g1)
    c: Distance(g1) = 2.7
    c: Coincident(g1,g0)
    c: Block(g0)
    c: Coincident(g2,g0)
    c: Vertical(g2)
    c: Horizontal(g3)
    c: Coincident(g3,g2)
    c: Horizontal(g4)
    c: Coincident(g5,g1)
    c: Vertical(g5)
    c: Coincident(g5,g4)
    c: Block(g3)
    c: Block(g4)
FEATURE [Sketcher::SketchObject] Sketch024
  FullyConstrained = true
  Placement = pos=(0,-14.3,2.37) rot=(-1,0,0;2.03453rad)
  sketch-geometry (4):
    g0: LineSegment StartX=49.5 StartY=-21.2 StartZ=0 EndX=49.5 EndY=-22.8 EndZ=0
    g1: LineSegment StartX=49.5 StartY=-22.8 StartZ=0 EndX=0.002238 EndY=-22.8 EndZ=0
    g2: LineSegment StartX=0.002238 StartY=-21.2 StartZ=0 EndX=0.002238 EndY=-22.8 EndZ=0
    g3: LineSegment StartX=49.5 StartY=-21.2 StartZ=0 EndX=0.002238 EndY=-21.2 EndZ=0
  constraints (10):
    c: Vertical(g0)
    c: Distance(g0) = 1.6
    c: Coincident(g1,g0)
    c: Horizontal(g1)
    c: Vertical(g2)
    c: Coincident(g2,g1)
    c: Coincident(g3,g0)
    c: Coincident(g3,g2)
    c: Horizontal(g3)
    c: Block(g3)
FEATURE [Sketcher::SketchObject] Sketch025
  FullyConstrained = true
  Placement = pos=(0,-14.3,2.37) rot=(-1,0,0;2.03453rad)
  sketch-geometry (4):
    g0: LineSegment StartX=0 StartY=1.5 StartZ=0 EndX=0 EndY=0 EndZ=0
    g1: LineSegment StartX=0 StartY=1.5 StartZ=0 EndX=5 EndY=1.5 EndZ=0
    g2: LineSegment StartX=5 StartY=1.5 StartZ=0 EndX=5 EndY=0 EndZ=0
    g3: LineSegment StartX=0 StartY=0 StartZ=0 EndX=5 EndY=0 EndZ=0
  constraints (13):
    c: Vertical(g0)
    c: Distance(g0) = 1.5
    c: Horizontal(g1)
    c: Distance(g1) = 5
    c: Coincident(g1,g0)
    c: Vertical(g2)
    c: Distance(g2) = 1.5
    c: Coincident(g2,g1)
    c: Block(g1)
    c: Block(g2)
    c: Block(g0)
    c: Coincident(g3,g0)
    c: Coincident(g3,g2)
FEATURE [Part::Extrusion] Extrude022  label="solenoidDriverBottomLipTopExtrude014"
  Base = -> Sketch025
  Dir = (0,0.894389,-0.447291)
  DirMode = 2
  FaceMakerClass = Part::FaceMakerBullseye
  LengthFwd = -6.5
  LengthRev = 0
  Placement = pos=(0,-15.45,20.3) rot=(1,0,0;1.5708rad)
  Solid = true
  Symmetric = false
FEATURE [Part::Fillet] Fillet013  label="solenoidDriverBottomLipTopFillet006"
  Base = -> Extrude022
  Edges = 1 edges r=1.4: [Edge6]
  Placement = pos=(5,0,0) rot=(0,0,1;0rad)
FEATURE [Sketcher::SketchObject] Sketch026
  FullyConstrained = true
  Placement = pos=(0,-14.3,2.37) rot=(-1,0,0;2.03453rad)
  sketch-geometry (4):
    g0: LineSegment StartX=0 StartY=1.5 StartZ=0 EndX=0 EndY=0 EndZ=0
    g1: LineSegment StartX=0 StartY=1.5 StartZ=0 EndX=5 EndY=1.5 EndZ=0
    g2: LineSegment StartX=5 StartY=1.5 StartZ=0 EndX=5 EndY=0 EndZ=0
    g3: LineSegment StartX=0 StartY=0 StartZ=0 EndX=5 EndY=0 EndZ=0
  constraints (13):
    c: Vertical(g0)
    c: Distance(g0) = 1.5
    c: Horizontal(g1)
    c: Distance(g1) = 5
    c: Coincident(g1,g0)
    c: Vertical(g2)
    c: Distance(g2) = 1.5
    c: Coincident(g2,g1)
    c: Block(g1)
    c: Block(g2)
    c: Block(g0)
    c: Coincident(g3,g0)
    c: Coincident(g3,g2)
FEATURE [Part::Extrusion] Extrude023  label="solenoidDriverBottomLipTopExtrude015"
  Base = -> Sketch026
  Dir = (0,0.894389,-0.447291)
  DirMode = 2
  FaceMakerClass = Part::FaceMakerBullseye
  LengthFwd = -6.5
  LengthRev = 0
  Placement = pos=(5,-14.15,19.65) rot=(1,0,0;1.5708rad)
  Solid = true
  Symmetric = false
FEATURE [Sketcher::SketchObject] Sketch027
  FullyConstrained = true
  Placement = pos=(0,-14.3,2.37) rot=(-1,0,0;2.03453rad)
  sketch-geometry (5):
    g0: LineSegment StartX=45.5 StartY=-21.2 StartZ=0 EndX=49.5 EndY=-21.2 EndZ=0
    g1: LineSegment StartX=49.5 StartY=0 StartZ=0 EndX=49.5 EndY=-21.2 EndZ=0
    g2: LineSegment StartX=49.5 StartY=0 StartZ=0 EndX=49.5 EndY=1.6 EndZ=0
    g3: LineSegment StartX=45.5 StartY=-21.2 StartZ=0 EndX=45.5 EndY=1.6 EndZ=0
    g4: LineSegment StartX=49.5 StartY=1.6 StartZ=0 EndX=45.5 EndY=1.6 EndZ=0
  constraints (14):
    c: Horizontal(g0)
    c: Distance(g0) = 4
    c: Coincident(g1,g0)
    c: Vertical(g1)
    c: Block(g1)
    c: Vertical(g2)
    c: Distance(g2) = 1.6
    c: Block(g2)
    c: Coincident(g3,g0)
    c: Vertical(g3)
    c: Coincident(g4,g2)
    c: Horizontal(g4)
    c: Block(g0)
    c: Coincident(g3,g4)
FEATURE [Part::Extrusion] Extrude024
  Base = -> Sketch027
  Dir = (0,0.894389,-0.447291)
  DirMode = 2
  FaceMakerClass = Part::FaceMakerBullseye
  LengthFwd = 6.34
  LengthRev = 0
  Placement = pos=(0,-5.59,1) rot=(0,0,1;0rad)
  Solid = true
  Symmetric = false
FEATURE [Part::Fillet] Fillet014  label="solenoidDriverSideBarFillet014"
  Base = -> Extrude024
  Edges = 1 edges r=1.4: [Edge14]
  Placement = pos=(0,0.9,-0.45) rot=(0,0,1;0rad)
FEATURE [Part::Revolution] Revolve  label="mainScrewStandRevolve"
  Angle = 360
  Axis = (0,0,1)
  Base = (0,0,0)
  FaceMakerClass = Part::FaceMakerBullseye
  Placement = pos=(121.35,-15.3,0) rot=(0,0,1;0rad)
  Solid = true
  Source = -> Sketch004
  Symmetric = false
FEATURE [Part::Extrusion] Extrude021  label="solenoidDriverTopLipLowerExtrude011"
  Base = -> Sketch024
  Dir = (0,0.894389,-0.447291)
  DirMode = 2
  FaceMakerClass = Part::FaceMakerBullseye
  LengthFwd = 5.05
  LengthRev = 0
  Solid = true
  Symmetric = false
FEATURE [Part::Fillet] Fillet012  label="solenoidDriverTopLipLowerFillet004"
  Base = -> Extrude021
  Edges = 1 edges r=1.2: [Edge7]
  Placement = pos=(0,-0.9,-1.35) rot=(0,0,1;0rad)
FEATURE [Part::Fillet] Fillet003  label="solenoidDriverTopLipLowerFillet003"
  Base = -> Extrude010
  Edges = 1 edges r=1.2: [Edge7]
  Placement = pos=(0,-3,-0.3) rot=(0,0,1;0rad)
FEATURE [Part::Extrusion] Extrude025  label="mainBodyUpperExtrude025"
  Base = -> Sketch001
  Dir = (0,0,1)
  DirMode = 2
  FaceMakerClass = Part::FaceMakerBullseye
  LengthFwd = 20
  LengthRev = 0
  Solid = true
  Symmetric = false
FEATURE [Part::MultiFuse] Fusion  label="solenoidDriverBottomLipFusion"
  Placement = pos=(0,-1.6,0) rot=(0,0,1;0rad)
  Shapes = -> [Fillet005,Fillet013,Extrude023,Extrude013]
FEATURE [Sketcher::SketchObject] Sketch028
  FullyConstrained = true
  Placement = pos=(0,-14.3,2.37) rot=(-1,0,0;2.03453rad)
  sketch-geometry (4):
    g0: LineSegment StartX=0 StartY=1.5 StartZ=0 EndX=0 EndY=0 EndZ=0
    g1: LineSegment StartX=0 StartY=1.5 StartZ=0 EndX=5 EndY=1.5 EndZ=0
    g2: LineSegment StartX=5 StartY=1.5 StartZ=0 EndX=5 EndY=0 EndZ=0
    g3: LineSegment StartX=0 StartY=0 StartZ=0 EndX=5 EndY=0 EndZ=0
  constraints (13):
    c: Vertical(g0)
    c: Distance(g0) = 1.5
    c: Horizontal(g1)
    c: Distance(g1) = 5
    c: Coincident(g1,g0)
    c: Vertical(g2)
    c: Distance(g2) = 1.5
    c: Coincident(g2,g1)
    c: Block(g1)
    c: Block(g2)
    c: Block(g0)
    c: Coincident(g3,g0)
    c: Coincident(g3,g2)
FEATURE [Part::Extrusion] Extrude026  label="solenoidDriverBottomLipTopExtrude016"
  Base = -> Sketch028
  Dir = (0,0.894389,-0.447291)
  DirMode = 2
  FaceMakerClass = Part::FaceMakerBullseye
  LengthFwd = -6.5
  LengthRev = 0
  Placement = pos=(5,-14.15,19.65) rot=(1,0,0;1.5708rad)
  Solid = true
  Symmetric = false
FEATURE [Sketcher::SketchObject] Sketch029
  FullyConstrained = true
  Placement = pos=(0,-14.3,2.37) rot=(-1,0,0;2.03453rad)
  sketch-geometry (4):
    g0: LineSegment StartX=0 StartY=1.5 StartZ=0 EndX=0 EndY=0 EndZ=0
    g1: LineSegment StartX=0 StartY=1.5 StartZ=0 EndX=5 EndY=1.5 EndZ=0
    g2: LineSegment StartX=5 StartY=1.5 StartZ=0 EndX=5 EndY=0 EndZ=0
    g3: LineSegment StartX=0 StartY=0 StartZ=0 EndX=5 EndY=0 EndZ=0
  constraints (13):
    c: Vertical(g0)
    c: Distance(g0) = 1.5
    c: Horizontal(g1)
    c: Distance(g1) = 5
    c: Coincident(g1,g0)
    c: Vertical(g2)
    c: Distance(g2) = 1.5
    c: Coincident(g2,g1)
    c: Block(g1)
    c: Block(g2)
    c: Block(g0)
    c: Coincident(g3,g0)
    c: Coincident(g3,g2)
FEATURE [Part::Extrusion] Extrude027  label="solenoidDriverBottomLipTopExtrude017"
  Base = -> Sketch029
  Dir = (0,0.894389,-0.447291)
  DirMode = 2
  FaceMakerClass = Part::FaceMakerBullseye
  LengthFwd = -6.5
  LengthRev = 0
  Placement = pos=(0,-14.15,19.65) rot=(1,0,0;1.5708rad)
  Solid = true
  Symmetric = false
FEATURE [Sketcher::SketchObject] Sketch030
  FullyConstrained = true
  Placement = pos=(0,-14.3,2.37) rot=(-1,0,0;2.03453rad)
  sketch-geometry (4):
    g0: LineSegment StartX=0 StartY=1.5 StartZ=0 EndX=0 EndY=0 EndZ=0
    g1: LineSegment StartX=0 StartY=1.5 StartZ=0 EndX=5 EndY=1.5 EndZ=0
    g2: LineSegment StartX=5 StartY=1.5 StartZ=0 EndX=5 EndY=0 EndZ=0
    g3: LineSegment StartX=0 StartY=0 StartZ=0 EndX=5 EndY=0 EndZ=0
  constraints (13):
    c: Vertical(g0)
    c: Distance(g0) = 1.5
    c: Horizontal(g1)
    c: Distance(g1) = 5
    c: Coincident(g1,g0)
    c: Vertical(g2)
    c: Distance(g2) = 1.5
    c: Coincident(g2,g1)
    c: Block(g1)
    c: Block(g2)
    c: Block(g0)
    c: Coincident(g3,g0)
    c: Coincident(g3,g2)
FEATURE [Sketcher::SketchObject] Sketch031
  FullyConstrained = true
  Placement = pos=(0,-14.3,2.37) rot=(-1,0,0;2.03453rad)
  sketch-geometry (6):
    g0: LineSegment StartX=45.5 StartY=-21.2 StartZ=0 EndX=49.5 EndY=-21.2 EndZ=0
    g1: LineSegment StartX=45.5 StartY=0 StartZ=0 EndX=49.5 EndY=0 EndZ=0
    g2: LineSegment StartX=49.5 StartY=0 StartZ=0 EndX=49.5 EndY=-21.2 EndZ=0
    g3: LineSegment StartX=4 StartY=0 StartZ=0 EndX=4 EndY=-21.2 EndZ=0
    g4: LineSegment StartX=45.5 StartY=-21.2 StartZ=0 EndX=4 EndY=-21.2 EndZ=0
    g5: LineSegment StartX=4 StartY=0 StartZ=0 EndX=45.5 EndY=0 EndZ=0
  constraints (16):
    c: Horizontal(g0)
    c: Distance(g0) = 4
    c: Horizontal(g1)
    c: Distance(g1) = 4
    c: Coincident(g2,g1)
    c: Coincident(g2,g0)
    c: Vertical(g2)
    c: Block(g2)
    c: Vertical(g3)
    c: Coincident(g4,g0)
    c: Horizontal(g4)
    c: Coincident(g4,g3)
    c: Coincident(g5,g1)
    c: Horizontal(g5)
    c: Block(g3)
    c: Block(g5)
FEATURE [Part::Extrusion] Extrude028  label="removeFromSolenoidDriverMainExtrude021"
  Base = -> Sketch031
  Dir = (0,0.894389,-0.447291)
  DirMode = 2
  FaceMakerClass = Part::FaceMakerBullseye
  LengthFwd = 3.1
  LengthRev = 0
  Placement = pos=(-4,-2.42,-0.8) rot=(0,0,1;0rad)
  Solid = true
  Symmetric = false
FEATURE [Part::Extrusion] Extrude029  label="solenoidDriverBottomLipTopExtrude018"
  Base = -> Sketch030
  Dir = (0,0.894389,-0.447291)
  DirMode = 2
  FaceMakerClass = Part::FaceMakerBullseye
  LengthFwd = -6.5
  LengthRev = 0
  Placement = pos=(5,-14.15,19.65) rot=(1,0,0;1.5708rad)
  Solid = true
  Symmetric = false
FEATURE [Sketcher::SketchObject] Sketch032
  FullyConstrained = true
  Placement = pos=(0,-14.3,2.37) rot=(-1,0,0;2.03453rad)
  sketch-geometry (4):
    g0: LineSegment StartX=0 StartY=1.5 StartZ=0 EndX=0 EndY=0 EndZ=0
    g1: LineSegment StartX=0 StartY=1.5 StartZ=0 EndX=5 EndY=1.5 EndZ=0
    g2: LineSegment StartX=5 StartY=1.5 StartZ=0 EndX=5 EndY=0 EndZ=0
    g3: LineSegment StartX=0 StartY=0 StartZ=0 EndX=5 EndY=0 EndZ=0
  constraints (13):
    c: Vertical(g0)
    c: Distance(g0) = 1.5
    c: Horizontal(g1)
    c: Distance(g1) = 5
    c: Coincident(g1,g0)
    c: Vertical(g2)
    c: Distance(g2) = 1.5
    c: Coincident(g2,g1)
    c: Block(g1)
    c: Block(g2)
    c: Block(g0)
    c: Coincident(g3,g0)
    c: Coincident(g3,g2)
FEATURE [Part::Extrusion] Extrude030  label="solenoidDriverBottomLipTopExtrude019"
  Base = -> Sketch032
  Dir = (0,0.894389,-0.447291)
  DirMode = 2
  FaceMakerClass = Part::FaceMakerBullseye
  LengthFwd = -6.5
  LengthRev = 0
  Placement = pos=(0,-14.15,19.65) rot=(1,0,0;1.5708rad)
  Solid = true
  Symmetric = false
FEATURE [Part::MultiFuse] Fusion004
  Placement = pos=(0,1.4,2.65) rot=(0,0,1;0rad)
  Shapes = -> [Extrude029,Extrude030]
FEATURE [Part::MultiFuse] Fusion003
  Placement = pos=(-2.3,0,0) rot=(0,0,1;0rad)
  Shapes = -> [Extrude028,Fusion004]
FEATURE [Sketcher::SketchObject] Sketch033
  FullyConstrained = true
  Placement = pos=(0,-14.3,2.37) rot=(-1,0,0;2.03453rad)
  sketch-geometry (4):
    g0: LineSegment StartX=0 StartY=1.5 StartZ=0 EndX=0 EndY=0 EndZ=0
    g1: LineSegment StartX=0 StartY=1.5 StartZ=0 EndX=5 EndY=1.5 EndZ=0
    g2: LineSegment StartX=5 StartY=1.5 StartZ=0 EndX=5 EndY=0 EndZ=0
    g3: LineSegment StartX=0 StartY=0 StartZ=0 EndX=5 EndY=0 EndZ=0
  constraints (13):
    c: Vertical(g0)
    c: Distance(g0) = 1.5
    c: Horizontal(g1)
    c: Distance(g1) = 5
    c: Coincident(g1,g0)
    c: Vertical(g2)
    c: Distance(g2) = 1.5
    c: Coincident(g2,g1)
    c: Block(g1)
    c: Block(g2)
    c: Block(g0)
    c: Coincident(g3,g0)
    c: Coincident(g3,g2)
FEATURE [Sketcher::SketchObject] Sketch034
  FullyConstrained = true
  Placement = pos=(0,-14.3,2.37) rot=(-1,0,0;2.03453rad)
  sketch-geometry (4):
    g0: LineSegment StartX=0 StartY=1.5 StartZ=0 EndX=0 EndY=0 EndZ=0
    g1: LineSegment StartX=0 StartY=1.5 StartZ=0 EndX=5 EndY=1.5 EndZ=0
    g2: LineSegment StartX=5 StartY=1.5 StartZ=0 EndX=5 EndY=0 EndZ=0
    g3: LineSegment StartX=0 StartY=0 StartZ=0 EndX=5 EndY=0 EndZ=0
  constraints (13):
    c: Vertical(g0)
    c: Distance(g0) = 1.5
    c: Horizontal(g1)
    c: Distance(g1) = 5
    c: Coincident(g1,g0)
    c: Vertical(g2)
    c: Distance(g2) = 1.5
    c: Coincident(g2,g1)
    c: Block(g1)
    c: Block(g2)
    c: Block(g0)
    c: Coincident(g3,g0)
    c: Coincident(g3,g2)
FEATURE [Part::Extrusion] Extrude020  label="removeFromSolenoidDriverMainExtrude020"
  Base = -> Sketch020
  Dir = (0,0.894389,-0.447291)
  DirMode = 2
  FaceMakerClass = Part::FaceMakerBullseye
  LengthFwd = 3.1
  LengthRev = 0
  Placement = pos=(-4,-2.42,-0.8) rot=(0,0,1;0rad)
  Solid = true
  Symmetric = false
FEATURE [Part::Fillet] Fillet
  Base = -> Fusion003
  Edges = 1 edges r=10: [Edge5]
  Placement = pos=(-2,0,0) rot=(0,0,1;0rad)
FEATURE [Part::MultiFuse] Fusion001
  Placement = pos=(0,1.4,2.65) rot=(0,0,1;0rad)
  Shapes = -> [Extrude026,Extrude027]
FEATURE [Part::MultiFuse] Fusion002
  Shapes = -> [Extrude020,Fusion001]
FEATURE [Sketcher::SketchObject] Sketch035
  FullyConstrained = true
  Placement = pos=(0,-14.3,2.37) rot=(-1,0,0;2.03453rad)
  sketch-geometry (4):
    g0: LineSegment StartX=0 StartY=1.5 StartZ=0 EndX=0 EndY=0 EndZ=0
    g1: LineSegment StartX=0 StartY=1.5 StartZ=0 EndX=5 EndY=1.5 EndZ=0
    g2: LineSegment StartX=5 StartY=1.5 StartZ=0 EndX=5 EndY=0 EndZ=0
    g3: LineSegment StartX=0 StartY=0 StartZ=0 EndX=5 EndY=0 EndZ=0
  constraints (13):
    c: Vertical(g0)
    c: Distance(g0) = 1.5
    c: Horizontal(g1)
    c: Distance(g1) = 5
    c: Coincident(g1,g0)
    c: Vertical(g2)
    c: Distance(g2) = 1.5
    c: Coincident(g2,g1)
    c: Block(g1)
    c: Block(g2)
    c: Block(g0)
    c: Coincident(g3,g0)
    c: Coincident(g3,g2)
FEATURE [Sketcher::SketchObject] Sketch036
  FullyConstrained = true
  Placement = pos=(0,-14.3,2.37) rot=(-1,0,0;2.03453rad)
  sketch-geometry (4):
    g0: LineSegment StartX=0 StartY=1.5 StartZ=0 EndX=0 EndY=0 EndZ=0
    g1: LineSegment StartX=0 StartY=1.5 StartZ=0 EndX=5 EndY=1.5 EndZ=0
    g2: LineSegment StartX=5 StartY=1.5 StartZ=0 EndX=5 EndY=0 EndZ=0
    g3: LineSegment StartX=0 StartY=0 StartZ=0 EndX=5 EndY=0 EndZ=0
  constraints (13):
    c: Vertical(g0)
    c: Distance(g0) = 1.5
    c: Horizontal(g1)
    c: Distance(g1) = 5
    c: Coincident(g1,g0)
    c: Vertical(g2)
    c: Distance(g2) = 1.5
    c: Coincident(g2,g1)
    c: Block(g1)
    c: Block(g2)
    c: Block(g0)
    c: Coincident(g3,g0)
    c: Coincident(g3,g2)
FEATURE [Part::Extrusion] Extrude031  label="solenoidDriverBottomLipTopExtrude020"
  Base = -> Sketch035
  Dir = (0,0.894389,-0.447291)
  DirMode = 2
  FaceMakerClass = Part::FaceMakerBullseye
  LengthFwd = -6.5
  LengthRev = 0
  Placement = pos=(5,-14.15,19.65) rot=(1,0,0;1.5708rad)
  Solid = true
  Symmetric = false
FEATURE [Part::Extrusion] Extrude032  label="solenoidDriverBottomLipTopExtrude021"
  Base = -> Sketch036
  Dir = (0,0.894389,-0.447291)
  DirMode = 2
  FaceMakerClass = Part::FaceMakerBullseye
  LengthFwd = -6.5
  LengthRev = 0
  Placement = pos=(0,-14.15,19.65) rot=(1,0,0;1.5708rad)
  Solid = true
  Symmetric = false
FEATURE [Part::MultiFuse] Fusion009
  Placement = pos=(8,1.4,2.65) rot=(0,0,1;0rad)
  Shapes = -> [Extrude031,Extrude032]
FEATURE [Part::MultiFuse] Fusion010  label="removeFromSolenoidDriver"
  Shapes = -> [Fusion009,Fillet,Fusion002]
FEATURE [Sketcher::SketchObject] Sketch037
  FullyConstrained = true
  Placement = pos=(0,0,0) rot=(1,0,0;1.5708rad)
  sketch-geometry (4):
    g0: Circle CenterX=64.05 CenterY=16.5 CenterZ=0 NormalX=0 NormalY=0 NormalZ=1 AngleXU=0 Radius=2.7
    g1: Circle CenterX=64.05 CenterY=8.5 CenterZ=0 NormalX=0 NormalY=0 NormalZ=1 AngleXU=0 Radius=2.7
    g2: Circle CenterX=84.15 CenterY=8.5 CenterZ=0 NormalX=0 NormalY=0 NormalZ=1 AngleXU=0 Radius=2.7
    g3: Circle CenterX=84.15 CenterY=16.5 CenterZ=0 NormalX=0 NormalY=0 NormalZ=1 AngleXU=0 Radius=2.7
  constraints (4):
    c: Block(g2)
    c: Block(g3)
    c: Block(g0)
    c: Block(g1)
FEATURE [Part::Extrusion] Extrude033  label="removeFromMainBodyToCreateScrewHoleCounterSinks001"
  Base = -> Sketch037
  Dir = (0,-1,1.1e-15)
  DirMode = 2
  FaceMakerClass = Part::FaceMakerBullseye
  LengthFwd = 1.9
  LengthRev = 0
  Placement = pos=(0.8,0,0) rot=(0,0,1;0rad)
  Solid = true
  Symmetric = false
FEATURE [Part::MultiFuse] Fusion011  label="removeFromMainBodyToCreateScrewHoleCounterSinks001Fusion011"
  Shapes = -> [Extrude014,Extrude033]
FEATURE [Sketcher::SketchObject] Sketch038
  FullyConstrained = true
  Placement = pos=(0,-14.3,2.37) rot=(-1,0,0;2.03453rad)
  sketch-geometry (4):
    g0: LineSegment StartX=33.9 StartY=-9.7 StartZ=0 EndX=33.9 EndY=-1.5 EndZ=0
    g1: LineSegment StartX=33.9 StartY=-1.5 StartZ=0 EndX=44.5 EndY=-1.5 EndZ=0
    g2: LineSegment StartX=33.9 StartY=-9.7 StartZ=0 EndX=44.5 EndY=-9.7 EndZ=0
    g3: LineSegment StartX=44.5 StartY=-1.5 StartZ=0 EndX=44.5 EndY=-9.7 EndZ=0
  constraints (10):
    c: Vertical(g0)
    c: Coincident(g1,g0)
    c: Horizontal(g1)
    c: Block(g1)
    c: Block(g0)
    c: Coincident(g2,g0)
    c: Horizontal(g2)
    c: Coincident(g3,g1)
    c: Coincident(g3,g2)
    c: Vertical(g3)
FEATURE [Part::Extrusion] Extrude034
  Base = -> Sketch038
  Dir = (0,0.894389,-0.447291)
  DirMode = 2
  FaceMakerClass = Part::FaceMakerBullseye
  LengthFwd = 16
  LengthRev = 0
  Placement = pos=(0,-22,7) rot=(0,0,1;0rad)
  Solid = true
  Symmetric = false
FEATURE [Sketcher::SketchObject] Sketch039
  FullyConstrained = true
  Placement = pos=(0,-14.3,2.37) rot=(-1,0,0;2.03453rad)
  sketch-geometry (4):
    g0: LineSegment StartX=5.5 StartY=-7.7 StartZ=0 EndX=13.3 EndY=-7.7 EndZ=0
    g1: LineSegment StartX=13.3 StartY=-7.7 StartZ=0 EndX=13.3 EndY=-13.1 EndZ=0
    g2: LineSegment StartX=13.3 StartY=-13.1 StartZ=0 EndX=5.5 EndY=-13.1 EndZ=0
    g3: LineSegment StartX=5.5 StartY=-7.7 StartZ=0 EndX=5.5 EndY=-13.1 EndZ=0
  constraints (12):
    c: Horizontal(g0)
    c: Distance(g0) = 7.8
    c: Coincident(g1,g0)
    c: Vertical(g1)
    c: Distance(g1) = 5.4
    c: Coincident(g2,g1)
    c: Horizontal(g2)
    c: Vertical(g3)
    c: Coincident(g3,g2)
    c: Block(g0)
    c: Block(g2)
    c: Block(g3)
FEATURE [Part::Extrusion] Extrude035  label="removeToMakeHoleForConnectorExtrude035"
  Base = -> Sketch039
  Dir = (0,0.894389,-0.447291)
  DirMode = 2
  FaceMakerClass = Part::FaceMakerBullseye
  LengthFwd = 15
  LengthRev = 0
  Placement = pos=(-4,-22,9.6469) rot=(0,0,1;0rad)
  Solid = true
  Symmetric = false
FEATURE [App::MeasureDistance] Distance  label="Distance: 4.00 mm"
  Distance = 4.00184
  P1 = (119.349,-15.3,8)
  P2 = (123.351,-15.3,8)
FEATURE [App::MeasureDistance] Distance001  label="Distance: 3.80 mm"
  Distance = 3.8
  P1 = (119.45,-15.3,8)
  P2 = (123.25,-15.3,8)
FEATURE [Part::Fillet] Fillet015
  Base = -> Extrude009
  Edges = 1 edges r=1.59: [Edge7]
FEATURE [Part::Fillet] Fillet016
  Base = -> Extrude017
  Edges = 1 edges r=1.49: [Edge12]
FEATURE [Part::Fillet] Fillet017
  Base = -> Fillet016
  Edges = 1 edges r=1.45: [Edge8]
FEATURE [Part::MultiFuse] Fusion012  label="main"
  Shapes = -> [Extrude,Revolve,Extrude005,Fillet003,Fillet012,Fillet014,Extrude025,Fusion,Fillet015,Fillet017]
FEATURE [Part::Cut] Cut001
  Base = -> Fusion012
  Tool = -> Box003
FEATURE [Part::Cut] Cut002
  Base = -> Cut001
  Tool = -> Box002
FEATURE [Part::Cut] Cut003
  Base = -> Cut002
  Tool = -> Cut
FEATURE [Part::Cut] Cut004
  Base = -> Cut003
  Tool = -> Extrude019
FEATURE [Part::Cut] Cut005
  Base = -> Cut004
  Tool = -> Fusion011
FEATURE [Part::Cut] Cut006
  Base = -> Cut005
  Tool = -> Extrude004
FEATURE [Part::Cut] Cut007
  Base = -> Cut006
  Tool = -> Extrude015
FEATURE [Part::Cut] Cut008
  Base = -> Cut007
  Tool = -> Extrude008
FEATURE [Part::Cut] Cut009
  Base = -> Cut008
  Tool = -> Fusion010
FEATURE [App::MeasureDistance] Distance002  label="Distance: 2.05 mm"
  Distance = 2.05453
  P1 = (1.5,-23.0732,21.402)
  P2 = (6e-15,-23,20)
FEATURE [Part::Cut] Cut010
  Base = -> Cut009
  Tool = -> Extrude035
FEATURE [Part::Cut] Cut011
  Base = -> Cut010
  Tool = -> Extrude034
FEATURE [Part::Box] Box004  label="Cube004"
  AttacherType = Attacher::AttachEngine3D
  Height = 10
  Length = 200
  Placement = pos=(-30,0,0) rot=(0,0,1;0rad)
  Width = 10
FEATURE [Part::Fillet] Fillet020
  Base = -> Box004
  Edges = 1 edges r=3.6: [Edge12]
FEATURE [Part::Box] Box005  label="Cube005"
  AttacherType = Attacher::AttachEngine3D
  Height = 10
  Length = 198
  Placement = pos=(-30,0,0) rot=(0,0,1;0rad)
  Width = 10
FEATURE [Part::Cut] Cut012
  Base = -> Box005
  Tool = -> Fillet020
FEATURE [Part::Box] Box006  label="Cube006"
  AttacherType = Attacher::AttachEngine3D
  Height = 5
  Length = 200
  Placement = pos=(-30,6.4,10) rot=(1,0,0;0rad)
  Width = 5
FEATURE [Part::Box] Box007  label="Cube007"
  AttacherType = Attacher::AttachEngine3D
  Height = 5
  Length = 200
  Placement = pos=(-30,6.4,10) rot=(1,0,0;0.872665rad)
  Width = 5
FEATURE [Part::MultiFuse] Fusion013  label="removeFromMainFusion013"
  Placement = pos=(0,-10,10) rot=(0,0,1;0rad)
  Shapes = -> [Box007,Box006,Cut012]
FEATURE [Mesh::Feature] v0_98_Cut013  label="v0_98-Cut013"
FEATURE [App::MeasureDistance] Distance003  label="Distance: 7.18 mm"
  Distance = 7.17719
  P1 = (117.773,-15.3145,-2.4)
  P2 = (124.951,-15.2973,-2.4)
FEATURE [Sketcher::SketchObject] Sketch040
  FullyConstrained = true
  Placement = pos=(0,-14.3,2.37) rot=(-1,0,0;2.03453rad)
  sketch-geometry (4):
    g0: LineSegment StartX=0 StartY=1.5 StartZ=0 EndX=0 EndY=0 EndZ=0
    g1: LineSegment StartX=0 StartY=1.5 StartZ=0 EndX=5 EndY=1.5 EndZ=0
    g2: LineSegment StartX=5 StartY=1.5 StartZ=0 EndX=5 EndY=0 EndZ=0
    g3: LineSegment StartX=0 StartY=0 StartZ=0 EndX=5 EndY=0 EndZ=0
  constraints (13):
    c: Vertical(g0)
    c: Distance(g0) = 1.5
    c: Horizontal(g1)
    c: Distance(g1) = 5
    c: Coincident(g1,g0)
    c: Vertical(g2)
    c: Distance(g2) = 1.5
    c: Coincident(g2,g1)
    c: Block(g1)
    c: Block(g2)
    c: Block(g0)
    c: Coincident(g3,g0)
    c: Coincident(g3,g2)
FEATURE [Part::Extrusion] Extrude036
  Base = -> Sketch040
  Dir = (0,0.894389,-0.447291)
  DirMode = 2
  FaceMakerClass = Part::FaceMakerBullseye
  LengthFwd = 1.4
  LengthRev = 0
  Placement = pos=(0,8.25,17.58) rot=(0,0,1;0rad)
  Solid = true
  Symmetric = false
FEATURE [Sketcher::SketchObject] Sketch041
  FullyConstrained = true
  Placement = pos=(0,-14.3,2.37) rot=(-1,0,0;2.03453rad)
  sketch-geometry (4):
    g0: LineSegment StartX=0 StartY=1.5 StartZ=0 EndX=0 EndY=0 EndZ=0
    g1: LineSegment StartX=0 StartY=1.5 StartZ=0 EndX=5 EndY=1.5 EndZ=0
    g2: LineSegment StartX=5 StartY=1.5 StartZ=0 EndX=5 EndY=0 EndZ=0
    g3: LineSegment StartX=0 StartY=0 StartZ=0 EndX=5 EndY=0 EndZ=0
  constraints (13):
    c: Vertical(g0)
    c: Distance(g0) = 1.5
    c: Horizontal(g1)
    c: Distance(g1) = 5
    c: Coincident(g1,g0)
    c: Vertical(g2)
    c: Distance(g2) = 1.5
    c: Coincident(g2,g1)
    c: Block(g1)
    c: Block(g2)
    c: Block(g0)
    c: Coincident(g3,g0)
    c: Coincident(g3,g2)
FEATURE [Part::Extrusion] Extrude037
  Base = -> Sketch041
  Dir = (0,0.894389,-0.447291)
  DirMode = 2
  FaceMakerClass = Part::FaceMakerBullseye
  LengthFwd = 1.4
  LengthRev = 0
  Placement = pos=(0,6.11,13.33) rot=(0,0,1;0rad)
  Solid = true
  Symmetric = false
FEATURE [Part::MultiFuse] Fusion014  label="screwSpacerFusion014"
  Shapes = -> [Extrude037,Extrude036]
FEATURE [Sketcher::SketchObject] Sketch042
  FullyConstrained = true
  Placement = pos=(0,-14.3,2.37) rot=(-1,0,0;2.03453rad)
  sketch-geometry (4):
    g0: LineSegment StartX=0 StartY=1.5 StartZ=0 EndX=0 EndY=0 EndZ=0
    g1: LineSegment StartX=0 StartY=1.5 StartZ=0 EndX=5 EndY=1.5 EndZ=0
    g2: LineSegment StartX=5 StartY=1.5 StartZ=0 EndX=5 EndY=0 EndZ=0
    g3: LineSegment StartX=0 StartY=0 StartZ=0 EndX=5 EndY=0 EndZ=0
  constraints (13):
    c: Vertical(g0)
    c: Distance(g0) = 1.5
    c: Horizontal(g1)
    c: Distance(g1) = 5
    c: Coincident(g1,g0)
    c: Vertical(g2)
    c: Distance(g2) = 1.5
    c: Coincident(g2,g1)
    c: Block(g1)
    c: Block(g2)
    c: Block(g0)
    c: Coincident(g3,g0)
    c: Coincident(g3,g2)
FEATURE [Part::Extrusion] Extrude038
  Base = -> Sketch042
  Dir = (0,0.894389,-0.447291)
  DirMode = 2
  FaceMakerClass = Part::FaceMakerBullseye
  LengthFwd = 1.4
  LengthRev = 0
  Placement = pos=(0,8.459,18) rot=(0,0,1;0rad)
  Solid = true
  Symmetric = false
FEATURE [Part::MultiFuse] Fusion015  label="screwSpacerFusion014Fusion015"
  Placement = pos=(0,0.35,-0.18) rot=(0,0,1;0rad)
  Shapes = -> [Extrude038,Fusion014]
FEATURE [Part::Cylinder] Cylinder
  Angle = 360
  AttacherType = Attacher::AttachEngine3D
  Height = 10
  Placement = pos=(0,10,0) rot=(0,0,1;0rad)
  Radius = 1.5
FEATURE [Part::Cylinder] Cylinder001
  Angle = 360
  AttacherType = Attacher::AttachEngine3D
  Height = 10
  Placement = pos=(3,10,0) rot=(0,0,1;0rad)
  Radius = 1.5
FEATURE [Part::Box] Box008  label="Cube008"
  AttacherType = Attacher::AttachEngine3D
  Height = 10
  Length = 3
  Placement = pos=(0,8.5,0) rot=(0,0,1;0rad)
  Width = 3
FEATURE [Part::MultiFuse] Fusion016  label="holeForWireFusion016"
  Shapes = -> [Cylinder001,Box008,Cylinder]
FEATURE [Part::Box] Box009  label="Cube009"
  AttacherType = Attacher::AttachEngine3D
  Height = 10
  Length = 3
  Placement = pos=(0,8.5,0) rot=(0,0,1;0rad)
  Width = 3
FEATURE [Part::Cylinder] Cylinder002
  Angle = 360
  AttacherType = Attacher::AttachEngine3D
  Height = 10
  Placement = pos=(0,10,0) rot=(0,0,1;0rad)
  Radius = 1.5
FEATURE [Part::Cylinder] Cylinder003
  Angle = 360
  AttacherType = Attacher::AttachEngine3D
  Height = 10
  Placement = pos=(3,10,0) rot=(0,0,1;0rad)
  Radius = 1.5
FEATURE [Part::MultiFuse] Fusion017  label="holeForWireFusion017"
  Placement = pos=(0,0,10) rot=(0,0,1;0rad)
  Shapes = -> [Cylinder003,Box009,Cylinder002]
FEATURE [Part::MultiFuse] Fusion018  label="holeForWireFusion018"
  Placement = pos=(0,0,0) rot=(0,1,0;-1.5708rad)
  Shapes = -> [Fusion017,Fusion016]
FEATURE [Part::Box] Box010  label="Cube010"
  AttacherType = Attacher::AttachEngine3D
  Height = 0.1
  Length = 0.1
  Placement = pos=(-2,10,0) rot=(0,0.995037,0.099504;0rad)
  Width = 0.1
FEATURE [Part::MultiFuse] Fusion019
  Placement = pos=(0,10,0) rot=(1,0,0;1.5708rad)
  Shapes = -> [Box010,Fusion018]
FEATURE [Part::Box] Box011  label="Cube011"
  AttacherType = Attacher::AttachEngine3D
  Height = 0.1
  Length = 1.1
  Placement = pos=(-2,10,10) rot=(0,0.995037,0.099504;0rad)
  Width = 0.1
FEATURE [Part::MultiFuse] Fusion020
  Placement = pos=(0,0,0) rot=(0,1,0;0.349066rad)
  Shapes = -> [Box011,Fusion019]
FEATURE [Part::Box] Box012  label="Cube012"
  AttacherType = Attacher::AttachEngine3D
  Height = 0.1
  Length = 1.1
  Placement = pos=(-2,10,10) rot=(0,0.995037,0.099504;0rad)
  Width = 0.1
FEATURE [Part::MultiFuse] Fusion021
  Placement = pos=(0,30,0) rot=(0,0,1;-2.6529rad)
  Shapes = -> [Box012,Fusion020]
FEATURE [Part::Box] Box013  label="Cube013"
  AttacherType = Attacher::AttachEngine3D
  Height = 0.1
  Length = 1.1
  Placement = pos=(2,19,10) rot=(0,0.995037,0.099504;0rad)
  Width = 0.1
FEATURE [Part::MultiFuse] Fusion022  label="holeForWire"
  Placement = pos=(15,-49.8,-8.2) rot=(0,0,1;0rad)
  Shapes = -> [Box013,Fusion021]
FEATURE [Part::Cut] Cut013
  Base = -> Cut011
  Tool = -> Fusion013
FEATURE [Part::Cut] Cut014
  Base = -> Cut013
  Tool = -> Fusion022
